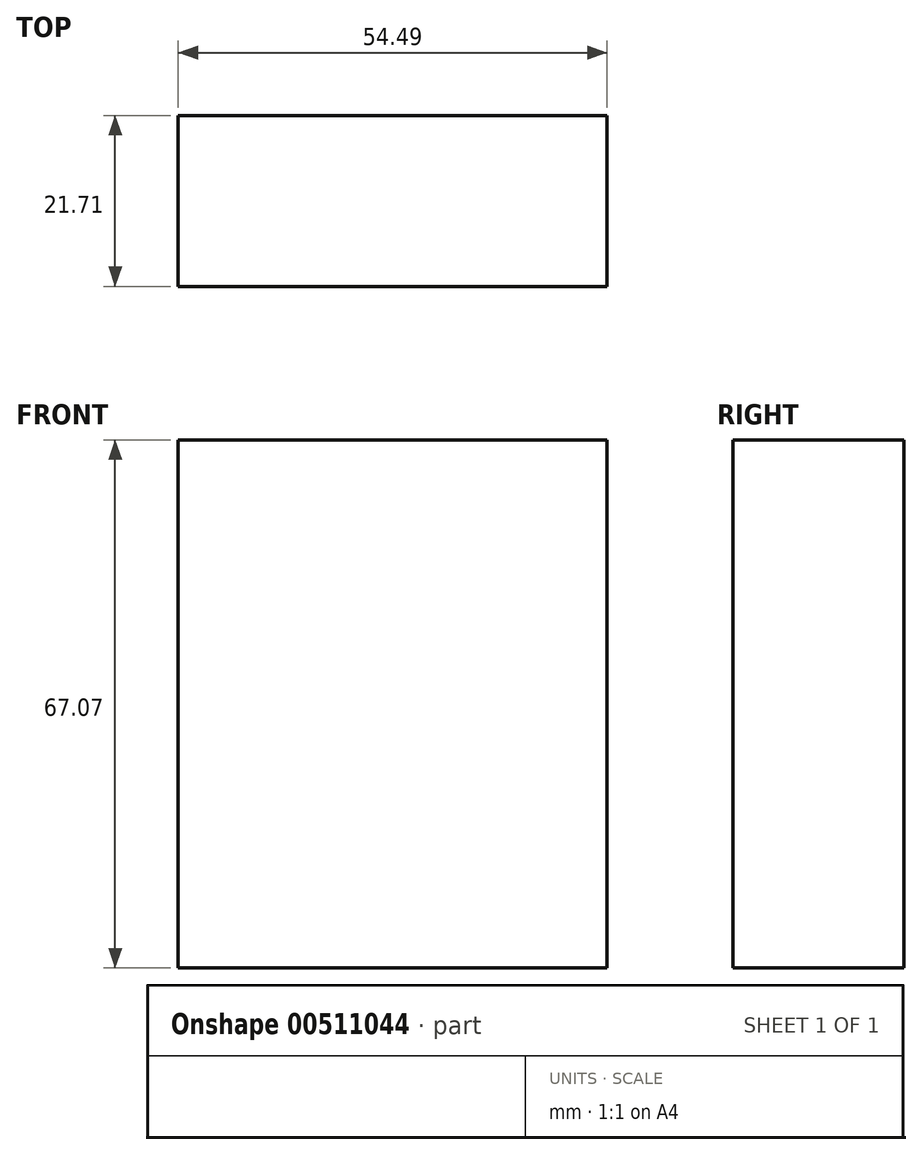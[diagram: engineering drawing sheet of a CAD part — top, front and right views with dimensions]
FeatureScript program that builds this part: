
annotation { "Feature Type Name" : "Feature", "Feature Type Description" : "" }
export const myFeature = defineFeature(function(context is Context, id is Id, definition is map)
    precondition{}
    {
        {
            var Q0;
            Q0=qCreatedBy(makeId("Front.planeOp"),FACE);
            var sketch = newSketch(context, id + "F0", { "sketchPlane" : qUnion([Q0])});
            skLineSegment(sketch, "E0.bottom", {"start": v(-25.27, 49.13) * mm, "end": v(-79.76, 49.13) * mm});
            skLineSegment(sketch, "E0.top", {"start": v(-25.27, -17.94) * mm, "end": v(-79.76, -17.94) * mm});
            skLineSegment(sketch, "E0.left", {"start": v(-25.27, 49.13) * mm, "end": v(-25.27, -17.94) * mm});
            skLineSegment(sketch, "E0.right", {"start": v(-79.76, 49.13) * mm, "end": v(-79.76, -17.94) * mm});
            skPoint(sketch, "E0.middle", {"position": v(-52.52, 15.6) * mm});
            skSolve(sketch);
        }
        {
            var Q0;
            Q0 = qSketchRegion(id + "F0", true);
            var Q1;
            Q1=makeQuery(id+"F0.imprint","IMPRINT",FACE,{"disambiguationData":[TD([[makeQuery(id+"F0.imprint","IMPRINT",EDGE,{"derivedFrom":sQuery(id+"F0.wireOp",EDGE,"E0.bottom")}),1.0]])]});
            extrude(context, id + "F1", {"entities" : qUnion([Q0, Q1]), "oppositeDirection" : true, "depth" : 21.7 * mm});
        }
    });
